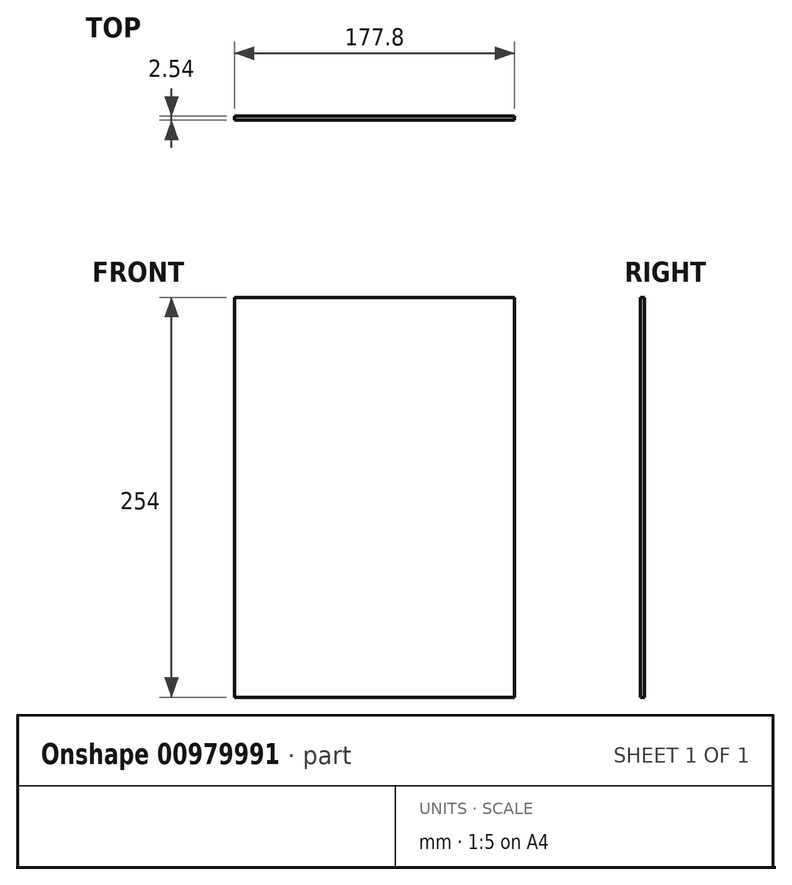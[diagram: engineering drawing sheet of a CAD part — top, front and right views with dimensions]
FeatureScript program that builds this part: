
annotation { "Feature Type Name" : "Feature", "Feature Type Description" : "" }
export const myFeature = defineFeature(function(context is Context, id is Id, definition is map)
    precondition{}
    {
        {
            var Q0;
            Q0=qCreatedBy(makeId("Front.planeOp"),FACE);
            var sketch = newSketch(context, id + "F0", { "sketchPlane" : qUnion([Q0])});
            skLineSegment(sketch, "E0.bottom", {"start": v(-138.07, 220.9) * mm, "end": v(39.73, 220.9) * mm});
            skLineSegment(sketch, "E0.top", {"start": v(-138.07, -33.1) * mm, "end": v(39.73, -33.1) * mm});
            skLineSegment(sketch, "E0.left", {"start": v(-138.07, 220.9) * mm, "end": v(-138.07, -33.1) * mm});
            skLineSegment(sketch, "E0.right", {"start": v(39.73, 220.9) * mm, "end": v(39.73, -33.1) * mm});
            skSolve(sketch);
        }
        {
            var Q0;
            Q0=makeQuery(id+"F0.imprint","IMPRINT",FACE,{"disambiguationData":[TD([[makeQuery(id+"F0.imprint","IMPRINT",EDGE,{"derivedFrom":sQuery(id+"F0.wireOp",EDGE,"E0.bottom")}),-1.0]])]});
            extrude(context, id + "F1", {"entities" : qUnion([Q0]), "depth" : 2.54 * mm, "offsetDistance" : 25.4 * mm});
        }
    });
